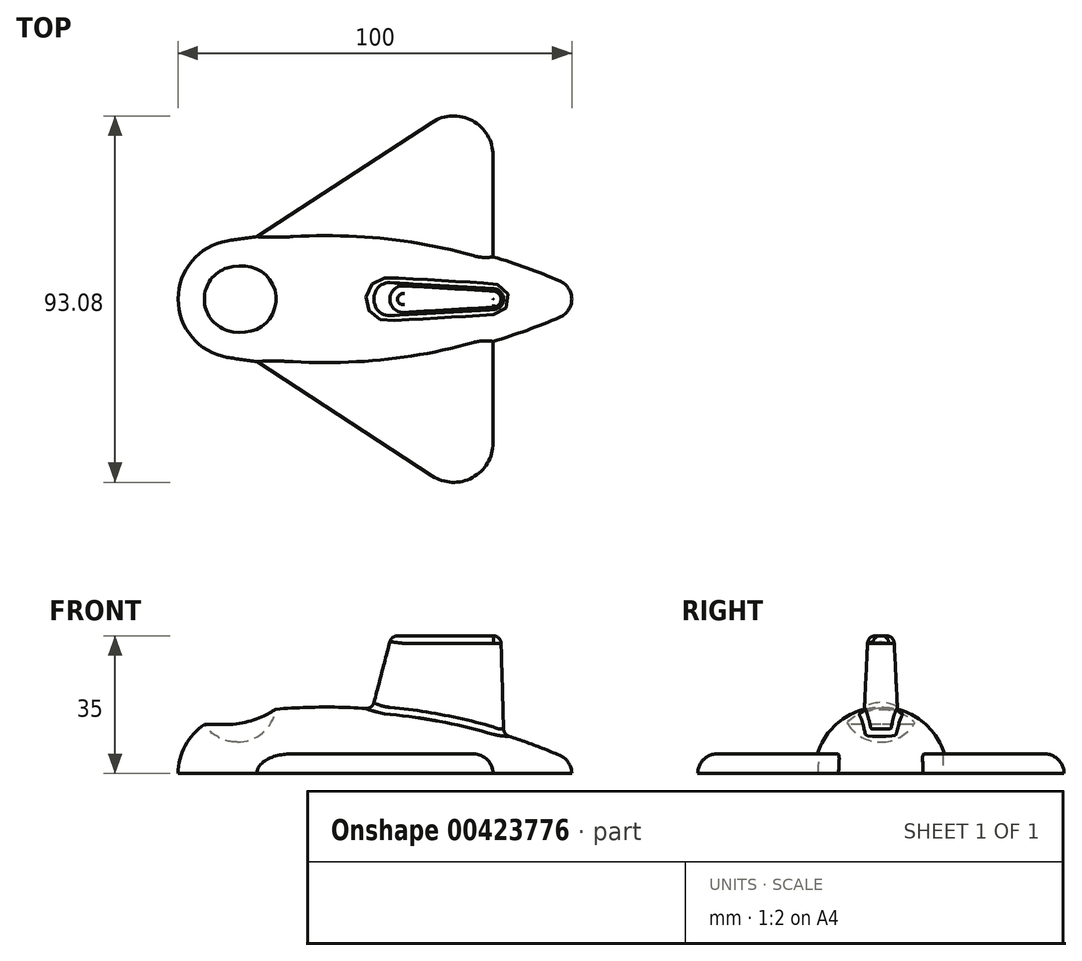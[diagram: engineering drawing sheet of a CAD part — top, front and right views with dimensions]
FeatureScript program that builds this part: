
annotation { "Feature Type Name" : "Feature", "Feature Type Description" : "" }
export const myFeature = defineFeature(function(context is Context, id is Id, definition is map)
    precondition{}
    {
        {
            var Q0;
            Q0=qCreatedBy(makeId("Top.planeOp"),FACE);
            var sketch = newSketch(context, id + "F0", { "sketchPlane" : qUnion([Q0])});
            skArc(sketch, "E0", {"start": v(-15, 0) * mm, "mid": v(-11.46, -9.68) * mm, "end": v(-2.5, -14.8) * mm});
            skArc(sketch, "E1", {"start": v(81.98, -4.6) * mm, "mid": v(84.18, -2.75) * mm, "end": v(85, 0) * mm});
            skArc(sketch, "E2.trimOffspring", {"start": v(81.98, -4.6) * mm, "mid": v(40.48, -15.8) * mm, "end": v(-2.5, -14.8) * mm});
            skLineSegment(sketch, "E3", {"start": v(-31.21, 0) * mm, "end": v(132.38, 0) * mm, "construction": true});
            skLineSegment(sketch, "E4", {"start": v(-15, 0) * mm, "end": v(85, 0) * mm});
            skSolve(sketch);
        }
        {
            var Q0;
            Q0=makeQuery(id+"F0.imprint","IMPRINT",FACE,{"disambiguationData":[TD([[makeQuery(id+"F0.imprint","IMPRINT",EDGE,{"derivedFrom":sQuery(id+"F0.wireOp",EDGE,"E0")}),1.0]])]});
            var Q1;
            Q1=sQuery(id+"F0.wireOp",EDGE,"E3");
            revolve(context, id + "F1", {"entities" : qUnion([Q0]), "axis" : qUnion([Q1]), "revolveType" : RevolveType.ONE_DIRECTION, "oppositeDirection" : true, "angle" : 180 * degree});
        }
        {
            var Q0;
            Q0=qCreatedBy(makeId("Front.planeOp"),FACE);
            var sketch = newSketch(context, id + "F2", { "sketchPlane" : qUnion([Q0])});
            skArc(sketch, "E5", {"start": v(0, 8) * mm, "mid": v(10, 18) * mm, "end": v(0, 28) * mm});
            skLineSegment(sketch, "E6", {"start": v(0, 8) * mm, "end": v(0, 28) * mm});
            skSolve(sketch);
        }
        {
            var Q0;
            Q0=makeQuery(id+"F2.imprint","IMPRINT",FACE,{"disambiguationData":[TD([[makeQuery(id+"F2.imprint","IMPRINT",EDGE,{"derivedFrom":sQuery(id+"F2.wireOp",EDGE,"E5")}),1.0]])]});
            var Q1;
            Q1=sQuery(id+"F2.wireOp",EDGE,"E6");
            revolve(context, id + "F3", {"operationType" : NewBodyOperationType.REMOVE, "entities" : qUnion([Q0]), "axis" : qUnion([Q1]), "revolveType" : RevolveType.FULL, "oppositeDirection" : true});
        }
        {
            var Q0;
            Q0=qCreatedBy(makeId("Top.planeOp"),FACE);
            var sketch = newSketch(context, id + "F4", { "sketchPlane" : qUnion([Q0])});
            skLineSegment(sketch, "E7", {"start": v(5, 15.86) * mm, "end": v(65, 55) * mm});
            skLineSegment(sketch, "E8", {"start": v(65, 55) * mm, "end": v(65, 0) * mm});
            skLineSegment(sketch, "E9", {"start": v(-19.32, 0) * mm, "end": v(65, 0) * mm});
            skLineSegment(sketch, "E10.MirrorCS", {"start": v(5, -15.86) * mm, "end": v(65, -55) * mm});
            skLineSegment(sketch, "E11.MirrorCS", {"start": v(65, -55) * mm, "end": v(65, 0) * mm});
            skArc(sketch, "E12.0", {"start": v(81.98, 4.6) * mm, "mid": v(40.48, 15.8) * mm, "end": v(-2.5, 14.8) * mm, "construction": true});
            skPoint(sketch, "E13.orphan", {"position": v(-19.32, 0) * mm});
            skLineSegment(sketch, "E14", {"start": v(5, 15.86) * mm, "end": v(-7.3, 7.85) * mm});
            skLineSegment(sketch, "E15", {"start": v(5, -15.86) * mm, "end": v(-5.2, -9.2) * mm});
            skLineSegment(sketch, "E16", {"start": v(-5.2, -9.2) * mm, "end": v(-7.3, 7.85) * mm});
            skSolve(sketch);
        }
        {
            var Q0;
            {var subQ0=sQuery(id+"F4.wireOp",EDGE,"E7");Q0=makeQuery(id+"F4.imprint","IMPRINT",FACE,{"disambiguationData":[TD([[makeQuery(id+"F4.imprint","IMPRINT",EDGE,{"derivedFrom":subQ0}),-1.0]])]});}
            var Q1;
            {var subQ4=sQuery(id+"F4.wireOp",EDGE,"E10.MirrorCS");Q1=makeQuery(id+"F4.imprint","IMPRINT",FACE,{"disambiguationData":[TD([[makeQuery(id+"F4.imprint","IMPRINT",EDGE,{"derivedFrom":subQ4}),1.0]])]});}
            extrude(context, id + "F5", {"entities" : qUnion([Q0, Q1]), "depth" : 5 * mm});
        }
        {
            var Q0;
            Q0=makeQuery(id+"F5.opExtrude","SWEPT_EDGE",EDGE,{"disambiguationData":[OSD([sQuery(id+"F4.wireOp",EDGE,"E7"),sQuery(id+"F4.wireOp",EDGE,"E8")])]});
            var Q1;
            Q1=makeQuery(id+"F5.opExtrude","SWEPT_EDGE",EDGE,{"disambiguationData":[OSD([sQuery(id+"F4.wireOp",EDGE,"E10.MirrorCS"),sQuery(id+"F4.wireOp",EDGE,"E11.MirrorCS")])]});
            fillet(context, id + "F6", {"entities" : qUnion([Q0, Q1]), "radius" : 10 * mm, "tangentPropagation" : true, "allowEdgeOverflow" : false});
        }
        {
            var Q0;
            Q0=makeQuery(id+"F5.opExtrude","CAP_EDGE",EDGE,{"disambiguationData":[OSD([sQuery(id+"F4.wireOp",EDGE,"E7"),sQuery(id+"F4.wireOp",EDGE,"E14")])],"isStart":false});
            fillet(context, id + "F7", {"entities" : qUnion([Q0]), "radius" : 5 * mm, "tangentPropagation" : true, "allowEdgeOverflow" : false});
        }
        {
            var Q0;
            Q0=qCreatedBy(makeId("Top.planeOp"),FACE);
            cPlane(context, id + "F8", {"entities" : qUnion([Q0]), "cplaneType" : CPlaneType.OFFSET, "offset" : 35 * mm, "width" : 150 * mm, "height" : 150 * mm});
        }
        {
            var Q0;
            Q0=qCreatedBy(id+"F8.planeOp",FACE);
            var sketch = newSketch(context, id + "F9", { "sketchPlane" : qUnion([Q0])});
            skArc(sketch, "E17", {"start": v(65.12, -2) * mm, "mid": v(67, 0) * mm, "end": v(65.12, 2) * mm});
            skArc(sketch, "E18", {"start": v(42.7, 3.3) * mm, "mid": v(39.2, 0) * mm, "end": v(42.7, -3.3) * mm});
            skLineSegment(sketch, "E19.0", {"start": v(65, 36.54) * mm, "end": v(65, -36.54) * mm, "construction": true});
            skLineSegment(sketch, "E20", {"start": v(42.7, -3.3) * mm, "end": v(65.12, -2) * mm});
            skLineSegment(sketch, "E21.MirrorCS", {"start": v(42.7, 3.3) * mm, "end": v(65.12, 2) * mm});
            skPoint(sketch, "E22.orphan", {"position": v(72.65, -1.56) * mm});
            skPoint(sketch, "E23.orphan", {"position": v(72.65, 1.56) * mm});
            skPoint(sketch, "E24.orphan", {"position": v(36.7, 3.64) * mm});
            skPoint(sketch, "E25.orphan", {"position": v(36.7, -3.64) * mm});
            skSolve(sketch);
        }
        {
            var Q0;
            Q0=qCreatedBy(makeId("Top.planeOp"),FACE);
            var sketch = newSketch(context, id + "F10", { "sketchPlane" : qUnion([Q0])});
            skArc(sketch, "E26", {"start": v(65.2, -3) * mm, "mid": v(68, 0) * mm, "end": v(65.2, 3) * mm});
            skArc(sketch, "E27", {"start": v(35.33, 4.99) * mm, "mid": v(30, 0) * mm, "end": v(35.33, -4.99) * mm});
            skLineSegment(sketch, "E28", {"start": v(35.33, 4.99) * mm, "end": v(65.2, 3) * mm});
            skLineSegment(sketch, "E29.MirrorCS", {"start": v(35.33, -4.99) * mm, "end": v(65.2, -3) * mm});
            skSolve(sketch);
        }
        {
            var Q0;
            Q0=makeQuery(id+"F9.imprint","IMPRINT",FACE,{"disambiguationData":[TD([[makeQuery(id+"F9.imprint","IMPRINT",EDGE,{"derivedFrom":sQuery(id+"F9.wireOp",EDGE,"E17")}),1.0]])]});
            var Q1;
            Q1=makeQuery(id+"F10.imprint","IMPRINT",FACE,{"disambiguationData":[TD([[makeQuery(id+"F10.imprint","IMPRINT",EDGE,{"derivedFrom":sQuery(id+"F10.wireOp",EDGE,"E26")}),1.0]])]});
            loft(context, id + "F11", {"sheetProfilesArray" : [{ "sheetProfileEntities" : qUnion([Q0]) }, { "sheetProfileEntities" : qUnion([Q1]) }]});
        }
        {
            var Q0;
            Q0=makeQuery(id+"F11.opLoft","CAP_FACE",FACE,{"disambiguationData":[OSD([makeQuery(id+"F9.imprint","IMPRINT",FACE,{"disambiguationData":[TD([[makeQuery(id+"F9.imprint","IMPRINT",EDGE,{"derivedFrom":sQuery(id+"F9.wireOp",EDGE,"E17")}),1.0]])]})])],"isStart":true});
            fillet(context, id + "F12", {"entities" : qUnion([Q0]), "radius" : 2 * mm, "tangentPropagation" : true, "allowEdgeOverflow" : false});
        }
        {
            var Q0;
            Q0=makeQuery(id+"F1.opRevolve","SWEPT_BODY",BODY,{"disambiguationData":[OSD([sQuery(id+"F0.wireOp",EDGE,"E0"),sQuery(id+"F0.wireOp",EDGE,"E1"),sQuery(id+"F0.wireOp",EDGE,"E2.trimOffspring"),sQuery(id+"F0.wireOp",EDGE,"E4")])]});
            var Q1;
            Q1=makeQuery(id+"F5.opExtrude","SWEPT_BODY",BODY,{"disambiguationData":[OSD([sQuery(id+"F4.wireOp",EDGE,"E7"),sQuery(id+"F4.wireOp",EDGE,"E8"),sQuery(id+"F4.wireOp",EDGE,"E10.MirrorCS"),sQuery(id+"F4.wireOp",EDGE,"E11.MirrorCS"),sQuery(id+"F4.wireOp",EDGE,"E14"),sQuery(id+"F4.wireOp",EDGE,"E15"),sQuery(id+"F4.wireOp",EDGE,"E16")])]});
            var Q2;
            Q2=makeQuery(id+"F11.opLoft","SWEPT_BODY",BODY,{"disambiguationData":[OSD([makeQuery(id+"F9.imprint","IMPRINT",FACE,{"disambiguationData":[TD([[makeQuery(id+"F9.imprint","IMPRINT",EDGE,{"derivedFrom":sQuery(id+"F9.wireOp",EDGE,"E17")}),1.0]])]}),makeQuery(id+"F10.imprint","IMPRINT",FACE,{"disambiguationData":[TD([[makeQuery(id+"F10.imprint","IMPRINT",EDGE,{"derivedFrom":sQuery(id+"F10.wireOp",EDGE,"E26")}),1.0]])]})])]});
            booleanBodies(context, id + "F13", {"operationType" : BooleanOperationType.UNION, "tools" : qUnion([Q0, Q1, Q2])});
        }
        {
            var Q0;
            Q0=makeQuery(id+"F13.opBoolean","INTERSECT",EDGE,{"derivedFrom":[makeQuery(id+"F1.opRevolve","SWEPT_FACE",FACE,{"disambiguationData":[OSD([sQuery(id+"F0.wireOp",EDGE,"E2.trimOffspring")])]}),makeQuery(id+"F11.opLoft","SWEPT_FACE",FACE,{"disambiguationData":[OSD([sQuery(id+"F9.wireOp",EDGE,"E17"),sQuery(id+"F9.wireOp",EDGE,"E18"),sQuery(id+"F9.wireOp",EDGE,"E20"),sQuery(id+"F10.wireOp",EDGE,"E26"),sQuery(id+"F10.wireOp",EDGE,"E27"),sQuery(id+"F10.wireOp",EDGE,"E29.MirrorCS")])]})]});
            fillet(context, id + "F14", {"entities" : qUnion([Q0]), "radius" : 2 * mm, "tangentPropagation" : true, "allowEdgeOverflow" : false});
        }
    });
